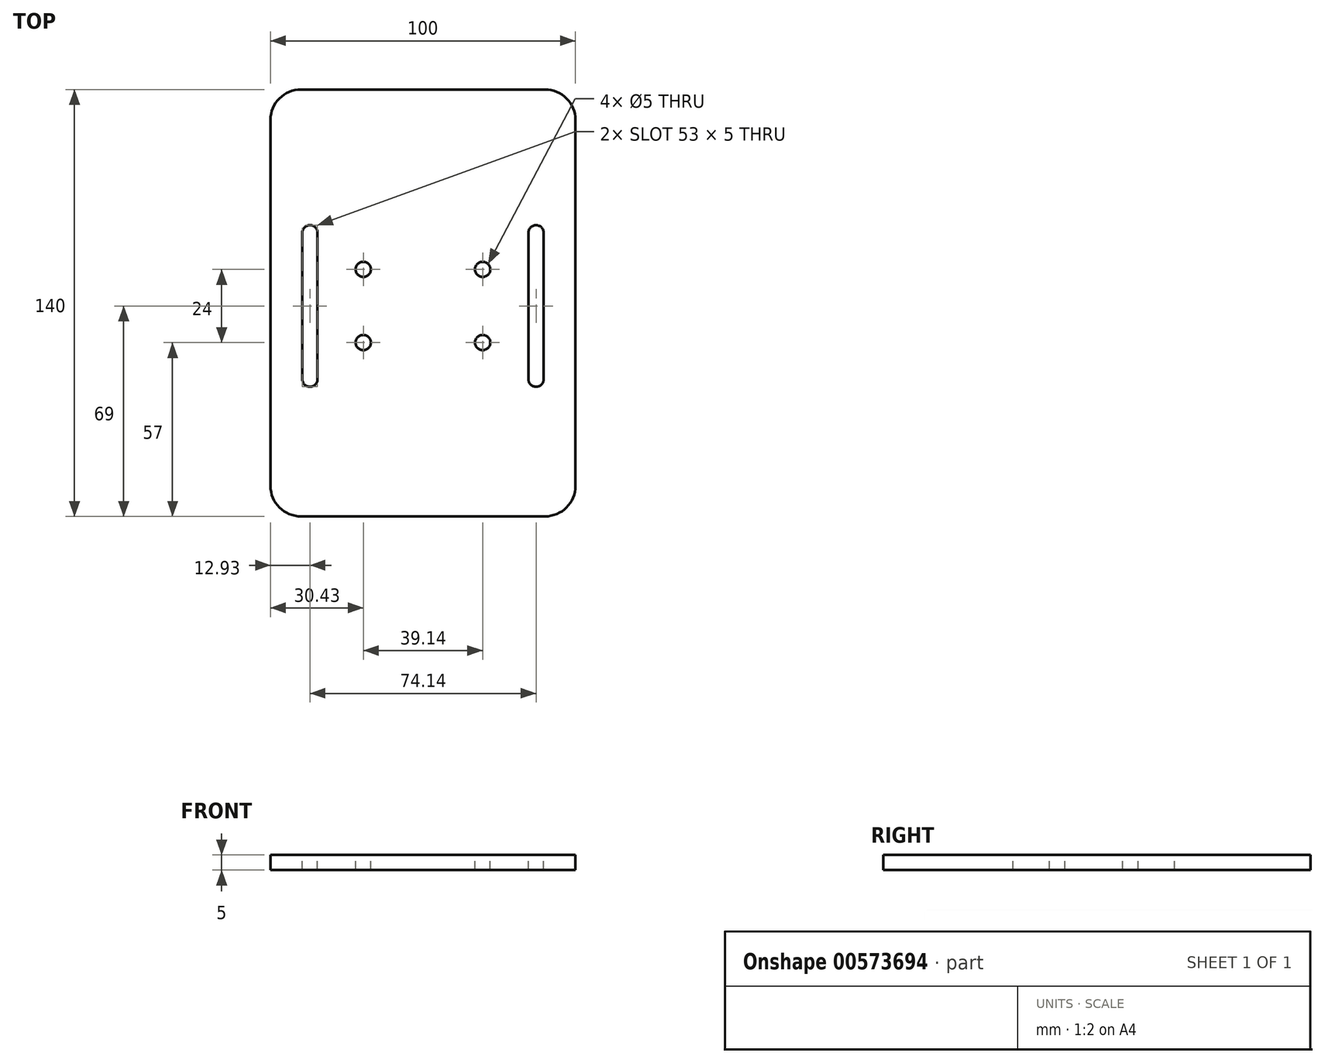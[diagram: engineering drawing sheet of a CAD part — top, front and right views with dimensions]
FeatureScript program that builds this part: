
annotation { "Feature Type Name" : "Feature", "Feature Type Description" : "" }
export const myFeature = defineFeature(function(context is Context, id is Id, definition is map)
    precondition{}
    {
        {
            var Q0;
            Q0=qCreatedBy(makeId("Top.planeOp"),FACE);
            var sketch = newSketch(context, id + "F0", { "sketchPlane" : qUnion([Q0])});
            skLineSegment(sketch, "E0.bottom", {"start": v(0, 0) * mm, "end": v(50, 0) * mm});
            skLineSegment(sketch, "E0.top", {"start": v(0, 140) * mm, "end": v(50, 140) * mm});
            skLineSegment(sketch, "E0.left", {"start": v(0, 0) * mm, "end": v(0, 140) * mm});
            skLineSegment(sketch, "E0.right", {"start": v(50, 0) * mm, "end": v(50, 140) * mm});
            skSolve(sketch);
        }
        {
            var Q0;
            Q0=makeQuery(id+"F0.imprint","IMPRINT",FACE,{"disambiguationData":[TD([[makeQuery(id+"F0.imprint","IMPRINT",EDGE,{"derivedFrom":sQuery(id+"F0.wireOp",EDGE,"E0.bottom")}),1.0]])]});
            extrude(context, id + "F1", {"entities" : qUnion([Q0]), "depth" : 5 * mm, "offsetDistance" : 25 * mm});
        }
        {
            var Q0;
            Q0=makeQuery(id+"F1.opExtrude","CAP_FACE",FACE,{"disambiguationData":[OSD([sQuery(id+"F0.wireOp",EDGE,"E0.bottom"),sQuery(id+"F0.wireOp",EDGE,"E0.top"),sQuery(id+"F0.wireOp",EDGE,"E0.left"),sQuery(id+"F0.wireOp",EDGE,"E0.right")])],"isStart":false});
            var sketch = newSketch(context, id + "F2", { "sketchPlane" : qUnion([Q0])});
            skSolve(sketch);
        }
        {
            var Q0;
            Q0=makeQuery(id+"F2.imprint","IMPRINT",FACE,{"disambiguationData":[TD([[makeQuery(id+"F2.imprint","IMPRINT",EDGE,{"derivedFrom":makeQuery(id+"F1.opExtrude","CAP_EDGE",EDGE,{"disambiguationData":[OSD([sQuery(id+"F0.wireOp",EDGE,"E0.bottom")])],"isStart":false})}),1.0]])]});
            var sketch = newSketch(context, id + "F3", { "sketchPlane" : qUnion([Q0])});
            skLineSegment(sketch, "E1", {"start": v(37.07, 45) * mm, "end": v(37.07, 93) * mm});
            skArc(sketch, "E2.0.startCap", {"start": v(39.57, 45) * mm, "mid": v(37.07, 42.5) * mm, "end": v(34.57, 45) * mm});
            skArc(sketch, "E2.0.endCap", {"start": v(34.57, 93) * mm, "mid": v(37.07, 95.5) * mm, "end": v(39.57, 93) * mm});
            skLineSegment(sketch, "E2.0.left", {"start": v(34.57, 45) * mm, "end": v(34.57, 93) * mm});
            skLineSegment(sketch, "E2.0.right", {"start": v(39.57, 45) * mm, "end": v(39.57, 93) * mm});
            skSolve(sketch);
        }
        {
            var Q0;
            Q0 = qSketchRegion(id + "F3", true);
            extrude(context, id + "F4", {"entities" : qUnion([Q0]), "operationType" : NewBodyOperationType.REMOVE, "oppositeDirection" : true, "depth" : 62.6 * mm, "offsetDistance" : 25 * mm});
        }
        {
            var Q0;
            Q0=makeQuery(id+"F2.imprint","IMPRINT",FACE,{"disambiguationData":[TD([[makeQuery(id+"F2.imprint","IMPRINT",EDGE,{"derivedFrom":makeQuery(id+"F1.opExtrude","CAP_EDGE",EDGE,{"disambiguationData":[OSD([sQuery(id+"F0.wireOp",EDGE,"E0.bottom")])],"isStart":false})}),1.0]])]});
            var sketch = newSketch(context, id + "F5", { "sketchPlane" : qUnion([Q0])});
            skLineSegment(sketch, "E3", {"start": v(19.57, 57) * mm, "end": v(19.57, 81) * mm});
            skSolve(sketch);
        }
        {
            var Q0;
            Q0=sQuery(id+"F5.wireOp",VERTEX,"E3.start");
            var Q1;
            Q1=sQuery(id+"F5.wireOp",VERTEX,"E3.end");
            var Q2;
            Q2=makeQuery(id+"F1.opExtrude","SWEPT_BODY",BODY,{"disambiguationData":[OSD([sQuery(id+"F0.wireOp",EDGE,"E0.bottom"),sQuery(id+"F0.wireOp",EDGE,"E0.top"),sQuery(id+"F0.wireOp",EDGE,"E0.left"),sQuery(id+"F0.wireOp",EDGE,"E0.right")])]});
            hole(context, id + "F6", {"style" : HoleStyle.SIMPLE, "endStyle" : HoleEndStyle.THROUGH, "holeDiameter" : 5 * mm, "isTappedThrough" : true, "tappedDepth" : 12 * mm, "tapClearance" : 3, "locations" : qUnion([Q0, Q1]), "scope" : qUnion([Q2])});
        }
        {
            var Q0;
            Q0=makeQuery(id+"F1.opExtrude","SWEPT_BODY",BODY,{"disambiguationData":[OSD([sQuery(id+"F0.wireOp",EDGE,"E0.bottom"),sQuery(id+"F0.wireOp",EDGE,"E0.top"),sQuery(id+"F0.wireOp",EDGE,"E0.left"),sQuery(id+"F0.wireOp",EDGE,"E0.right")])]});
            var Q1;
            Q1=qCreatedBy(makeId("Right.planeOp"),FACE);
            mirror(context, id + "F7", {"operationType" : NewBodyOperationType.ADD, "entities" : qUnion([Q0]), "mirrorPlane" : qUnion([Q1])});
        }
        {
            var Q0;
            Q0=makeQuery(id+"F1.opExtrude","SWEPT_EDGE",EDGE,{"disambiguationData":[OSD([sQuery(id+"F0.wireOp",EDGE,"E0.top"),sQuery(id+"F0.wireOp",EDGE,"E0.right")])]});
            fillet(context, id + "F8", {"entities" : qUnion([Q0]), "radius" : 10 * mm, "tangentPropagation" : true, "allowEdgeOverflow" : false});
        }
        {
            var Q0;
            Q0=makeQuery(id+"F1.opExtrude","SWEPT_EDGE",EDGE,{"disambiguationData":[OSD([sQuery(id+"F0.wireOp",EDGE,"E0.bottom"),sQuery(id+"F0.wireOp",EDGE,"E0.right")])]});
            fillet(context, id + "F9", {"entities" : qUnion([Q0]), "radius" : 10 * mm, "tangentPropagation" : true, "allowEdgeOverflow" : false});
        }
        {
            var Q0;
            Q0=makeQuery(id+"F7.opPattern","COPY",EDGE,{"derivedFrom":makeQuery(id+"F1.opExtrude","SWEPT_EDGE",EDGE,{"disambiguationData":[OSD([sQuery(id+"F0.wireOp",EDGE,"E0.bottom"),sQuery(id+"F0.wireOp",EDGE,"E0.right")])]}),"instanceName":"1"});
            fillet(context, id + "F10", {"entities" : qUnion([Q0]), "radius" : 10 * mm, "tangentPropagation" : true, "allowEdgeOverflow" : false});
        }
        {
            var Q0;
            Q0=makeQuery(id+"F7.opPattern","COPY",EDGE,{"derivedFrom":makeQuery(id+"F1.opExtrude","SWEPT_EDGE",EDGE,{"disambiguationData":[OSD([sQuery(id+"F0.wireOp",EDGE,"E0.top"),sQuery(id+"F0.wireOp",EDGE,"E0.right")])]}),"instanceName":"1"});
            fillet(context, id + "F11", {"entities" : qUnion([Q0]), "radius" : 10 * mm, "tangentPropagation" : true, "allowEdgeOverflow" : false});
        }
    });
